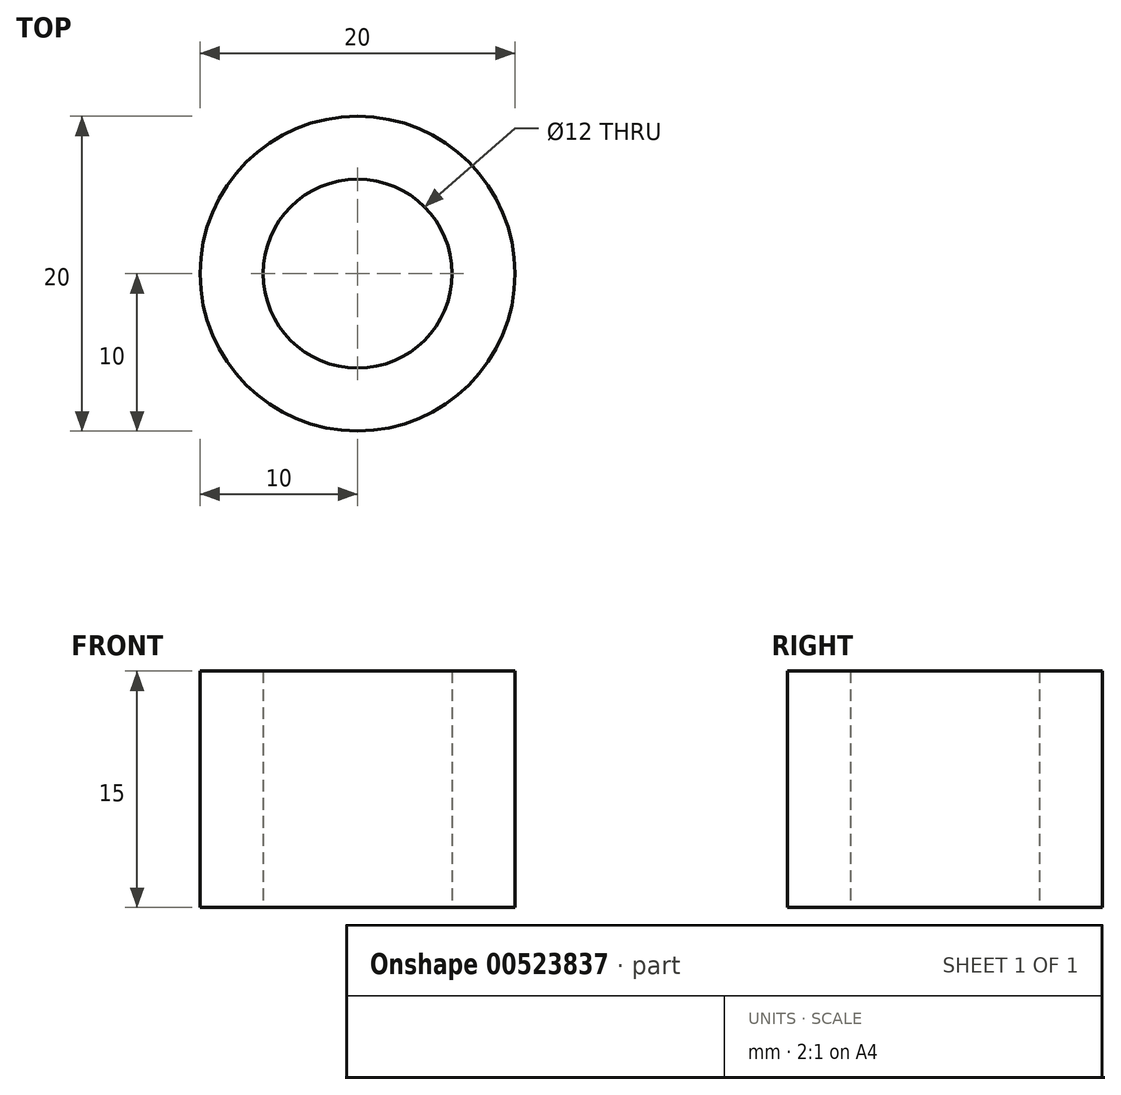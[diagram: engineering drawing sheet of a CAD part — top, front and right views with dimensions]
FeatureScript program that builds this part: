
annotation { "Feature Type Name" : "Feature", "Feature Type Description" : "" }
export const myFeature = defineFeature(function(context is Context, id is Id, definition is map)
    precondition{}
    {
        {
            var Q0;
            Q0=qCreatedBy(makeId("Top.planeOp"),FACE);
            var sketch = newSketch(context, id + "F0", { "sketchPlane" : qUnion([Q0])});
            skCircle(sketch, "E0", {"center": v(0, 0) * mm, "radius": 10 * mm});
            skSolve(sketch);
        }
        {
            var Q0;
            Q0=makeQuery(id+"F0.imprint","IMPRINT",FACE,{"disambiguationData":[TD([[makeQuery(id+"F0.imprint","IMPRINT",EDGE,{"derivedFrom":sQuery(id+"F0.wireOp",EDGE,"E0")}),1.0]])]});
            extrude(context, id + "F1", {"entities" : qUnion([Q0]), "depth" : 15 * mm, "offsetDistance" : 25 * mm});
        }
        {
            var Q0;
            Q0=makeQuery(id+"F1.opExtrude","CAP_FACE",FACE,{"disambiguationData":[OSD([sQuery(id+"F0.wireOp",EDGE,"E0")])],"isStart":false});
            var sketch = newSketch(context, id + "F2", { "sketchPlane" : qUnion([Q0])});
            skCircle(sketch, "E1", {"center": v(0, 0) * mm, "radius": 6 * mm});
            skSolve(sketch);
        }
        {
            var Q0;
            Q0=sQuery(id+"F2.wireOp",VERTEX,"E1.center");
            var Q1;
            Q1=makeQuery(id+"F1.opExtrude","SWEPT_BODY",BODY,{"disambiguationData":[OSD([sQuery(id+"F0.wireOp",EDGE,"E0")])]});
            hole(context, id + "F3", {"style" : HoleStyle.SIMPLE, "endStyle" : HoleEndStyle.THROUGH, "holeDiameter" : 12 * mm, "majorDiameter" : 5 * mm, "isTappedThrough" : true, "tappedDepth" : 12 * mm, "tapClearance" : 3, "locations" : qUnion([Q0]), "scope" : qUnion([Q1])});
        }
    });
